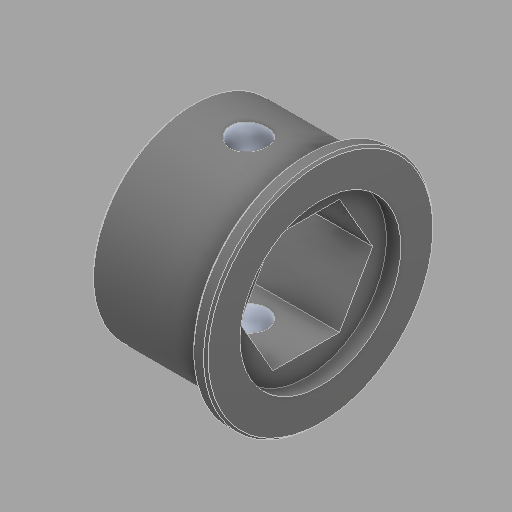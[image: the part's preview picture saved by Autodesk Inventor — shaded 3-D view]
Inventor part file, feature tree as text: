
AUTODESK INVENTOR PART (.ipt)
format: ipt  version: 2024.2 (Build 282272000, 272)  size: 153,600 bytes
history: native  units: in
note: dims shown in document units (in); Inventor stores cm internally (conversion verified against a paired STEP export)
features: chamfer x1
ambient origin geometry x8: Origin, YZ Plane, XZ Plane, XY Plane, X Axis, Y Axis, Z Axis, Center Point
bodies: Solid1 (feature_tree)
feature tree (1):
  chamfer  "Chamfer1"  [1 undecoded]
note: 1 required parameter value undecoded (feature->parameter linkage not recoverable at this tier; creation-order binding heuristic only, values carry confidence <= 0.55)
